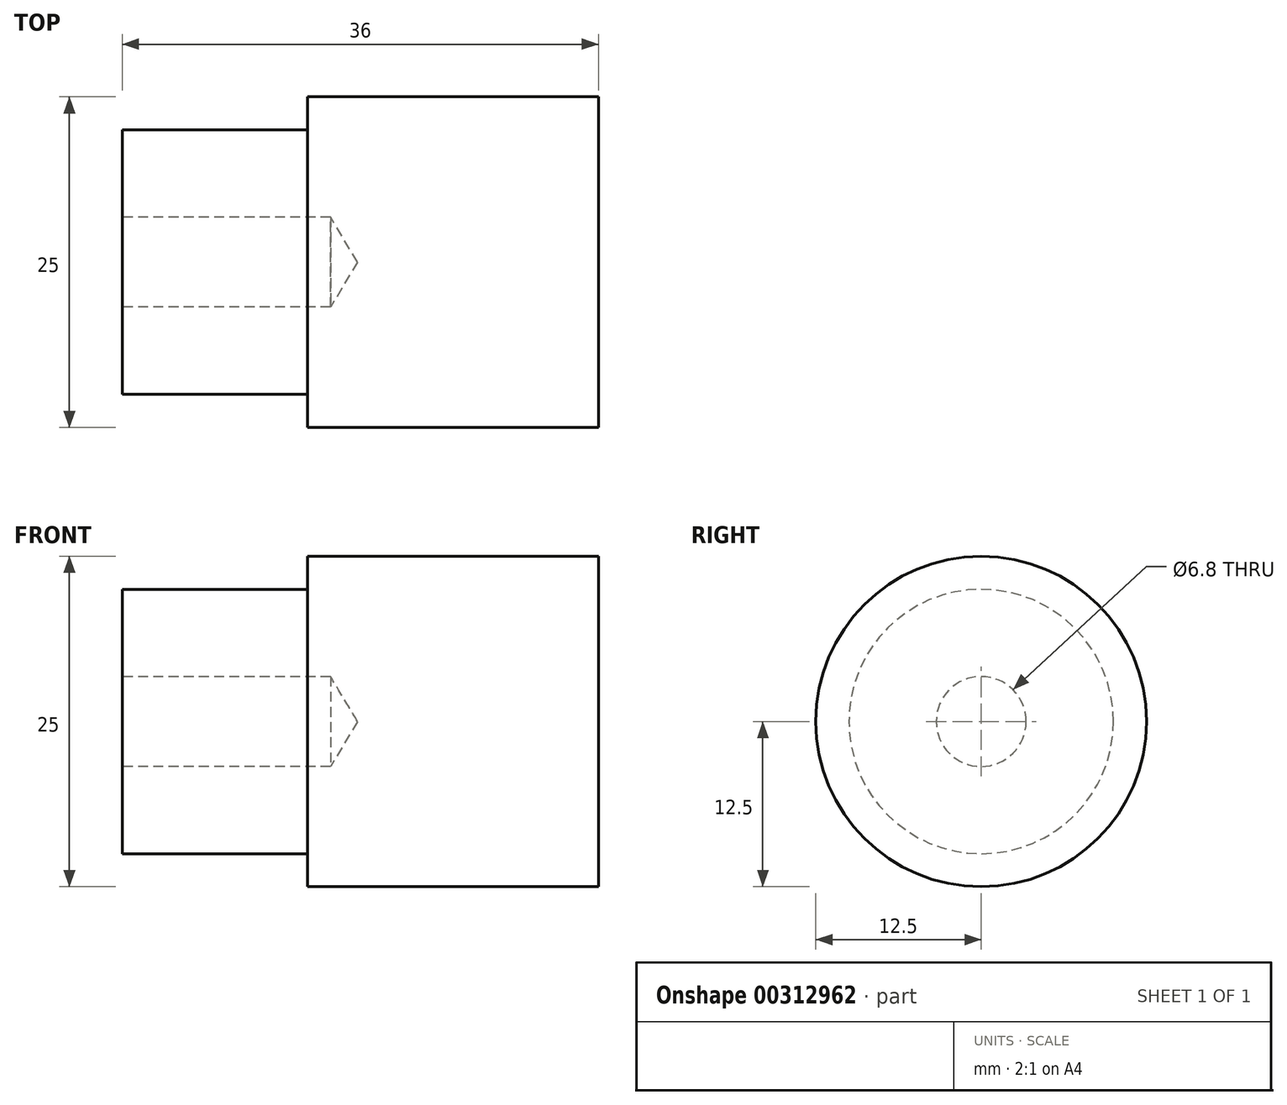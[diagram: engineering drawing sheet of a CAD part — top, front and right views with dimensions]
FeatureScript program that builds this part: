
annotation { "Feature Type Name" : "Feature", "Feature Type Description" : "" }
export const myFeature = defineFeature(function(context is Context, id is Id, definition is map)
    precondition{}
    {
        {
            var Q0;
            Q0=qCreatedBy(makeId("Front.planeOp"),FACE);
            var sketch = newSketch(context, id + "F0", { "sketchPlane" : qUnion([Q0])});
            skLineSegment(sketch, "E0", {"start": v(-36, 0) * mm, "end": v(0, 0) * mm});
            skLineSegment(sketch, "E1", {"start": v(0, 0) * mm, "end": v(0, 12.5) * mm});
            skLineSegment(sketch, "E2", {"start": v(0, 12.5) * mm, "end": v(-22, 12.5) * mm});
            skLineSegment(sketch, "E3", {"start": v(-22, 12.5) * mm, "end": v(-22, 10) * mm});
            skLineSegment(sketch, "E4", {"start": v(-22, 10) * mm, "end": v(-36, 10) * mm});
            skLineSegment(sketch, "E5", {"start": v(-36, 10) * mm, "end": v(-36, 0) * mm});
            skSolve(sketch);
        }
        {
            var Q0;
            Q0=makeQuery(id+"F0.imprint","IMPRINT",FACE,{"disambiguationData":[TD([[makeQuery(id+"F0.imprint","IMPRINT",EDGE,{"derivedFrom":sQuery(id+"F0.wireOp",EDGE,"E0")}),1.0]])]});
            var Q1;
            Q1=sQuery(id+"F0.wireOp",EDGE,"E0");
            revolve(context, id + "F1", {"entities" : qUnion([Q0]), "axis" : qUnion([Q1]), "revolveType" : RevolveType.FULL});
        }
        {
            var Q0;
            Q0=makeQuery(id+"F1.opRevolve","SWEPT_FACE",FACE,{"disambiguationData":[OSD([sQuery(id+"F0.wireOp",EDGE,"E5")])]});
            var sketch = newSketch(context, id + "F2", { "sketchPlane" : qUnion([Q0])});
            skPoint(sketch, "E6", {"position": v(0, 0) * mm});
            skSolve(sketch);
        }
        {
            var Q0;
            Q0=sQuery(id+"F2.wireOp",VERTEX,"E6");
            var Q1;
            Q1=makeQuery(id+"F1.opRevolve","SWEPT_BODY",BODY,{"disambiguationData":[OSD([sQuery(id+"F0.wireOp",EDGE,"E0"),sQuery(id+"F0.wireOp",EDGE,"E1"),sQuery(id+"F0.wireOp",EDGE,"E2"),sQuery(id+"F0.wireOp",EDGE,"E3"),sQuery(id+"F0.wireOp",EDGE,"E4"),sQuery(id+"F0.wireOp",EDGE,"E5")])]});
            hole(context, id + "F3", {"style" : HoleStyle.SIMPLE, "endStyle" : HoleEndStyle.BLIND, "standardTappedOrClearance" : lookupTablePath({ "standard" : "ISO", "engagement" : "75%", "pitch" : "1.25 mm", "size" : "M8", "type" : "Tapped" }), "standardBlindInLast" : lookupTablePath({ "standard" : "ISO", "engagement" : "75%", "pitch" : "1.25 mm", "size" : "M8", "type" : "Tapped" }), "holeDiameter" : 6.8 * mm, "showTappedDepth" : true, "holeDepth" : 15.75 * mm, "isTappedThrough" : true, "tappedDepth" : 12 * mm, "tapClearance" : 3, "locations" : qUnion([Q0]), "scope" : qUnion([Q1]), "majorDiameter" : 8 * mm});
        }
    });
